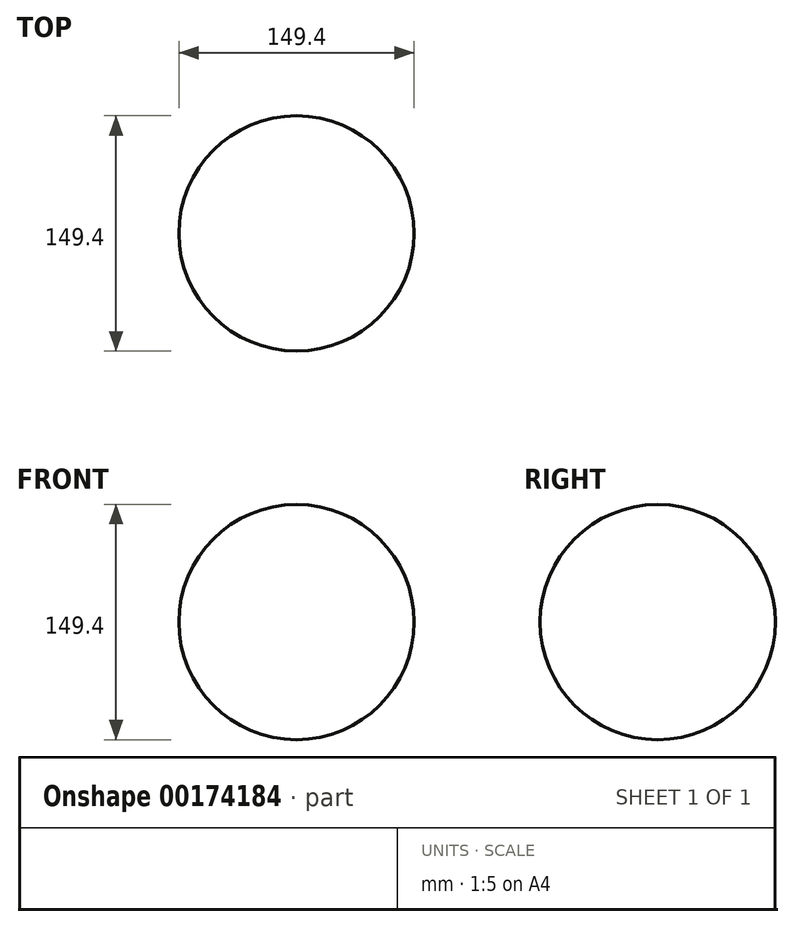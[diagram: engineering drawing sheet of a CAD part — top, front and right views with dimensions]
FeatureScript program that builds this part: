
annotation { "Feature Type Name" : "Feature", "Feature Type Description" : "" }
export const myFeature = defineFeature(function(context is Context, id is Id, definition is map)
    precondition{}
    {
        {
            var Q0;
            Q0=qCreatedBy(makeId("Front.planeOp"),FACE);
            var sketch = newSketch(context, id + "F0", { "sketchPlane" : qUnion([Q0])});
            skArc(sketch, "E0", {"start": v(0, 74.7) * mm, "mid": v(-74.7, 0) * mm, "end": v(0, -74.7) * mm});
            skLineSegment(sketch, "E1", {"start": v(0, 74.7) * mm, "end": v(0, -74.7) * mm});
            skSolve(sketch);
        }
        {
            var Q0;
            Q0=makeQuery(id+"F0.imprint","IMPRINT",FACE,{"disambiguationData":[TD([[makeQuery(id+"F0.imprint","IMPRINT",EDGE,{"derivedFrom":sQuery(id+"F0.wireOp",EDGE,"E0")}),1.0]])]});
            var Q1;
            Q1=sQuery(id+"F0.wireOp",EDGE,"E1");
            revolve(context, id + "F1", {"entities" : qUnion([Q0]), "axis" : qUnion([Q1]), "revolveType" : RevolveType.FULL});
        }
    });
